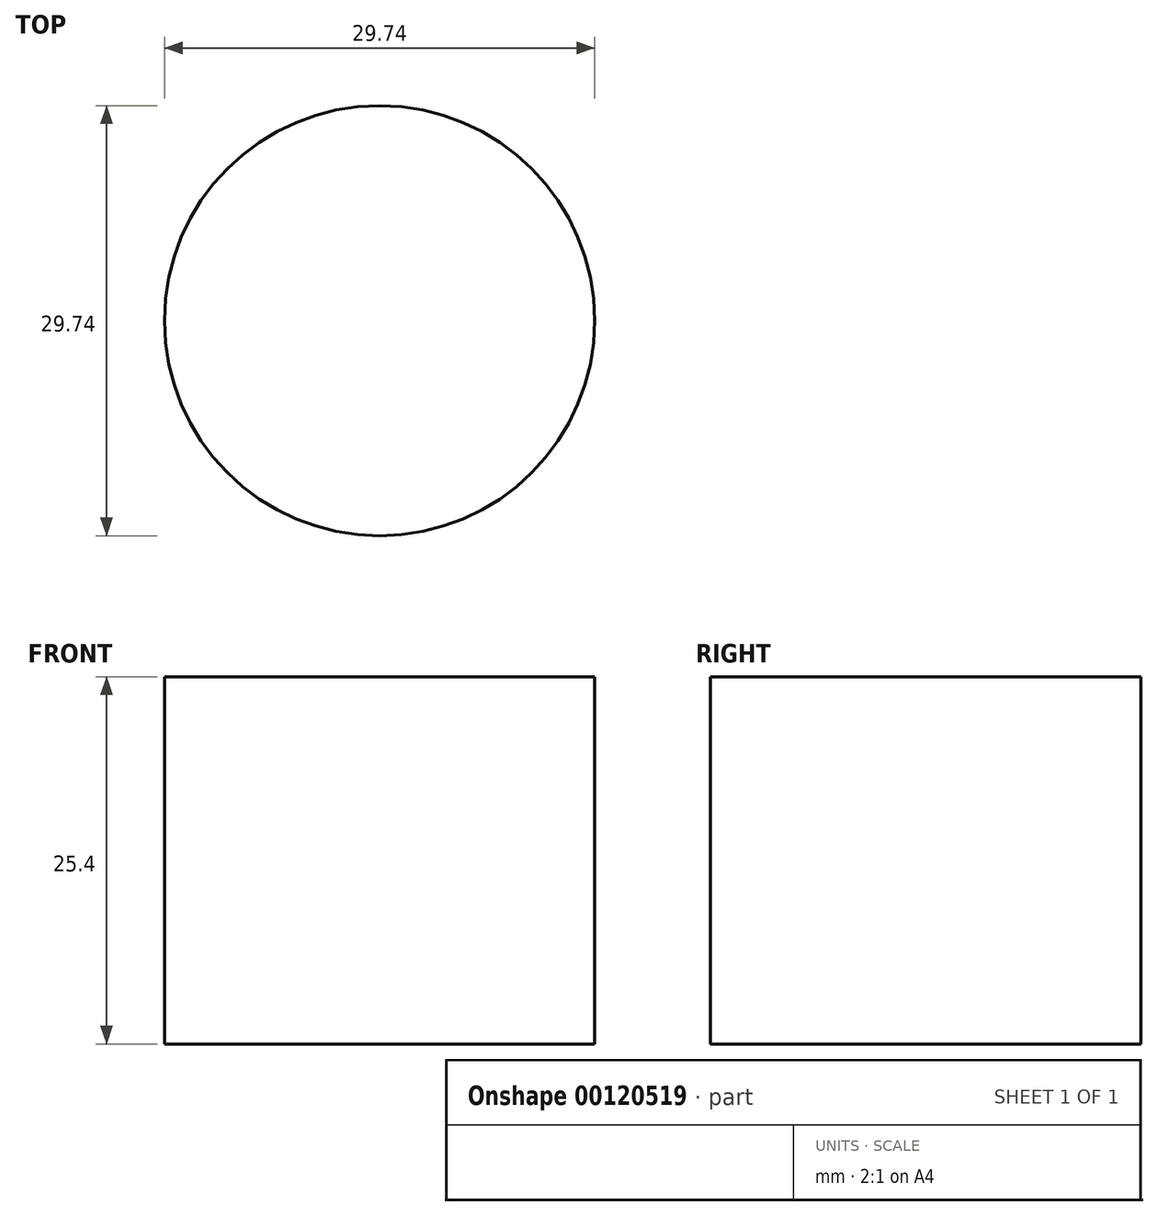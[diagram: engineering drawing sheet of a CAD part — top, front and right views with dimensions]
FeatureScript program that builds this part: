
annotation { "Feature Type Name" : "Feature", "Feature Type Description" : "" }
export const myFeature = defineFeature(function(context is Context, id is Id, definition is map)
    precondition{}
    {
        {
            var Q0;
            Q0=qCreatedBy(makeId("Top.planeOp"),FACE);
            var sketch = newSketch(context, id + "F0", { "sketchPlane" : qUnion([Q0])});
            skCircle(sketch, "E0", {"center": v(0, 0) * mm, "radius": 25.58 * mm});
            skSolve(sketch);
        }
        {
            var Q0;
            Q0 = qSketchRegion(id + "F0", true);
            var Q1;
            Q1=sQuery(id+"F0.wireOp",EDGE,"E0");
            extrude(context, id + "F1", {"entities" : qUnion([Q0]), "bodyType" : ToolBodyType.SURFACE, "surfaceEntities" : qUnion([Q1]), "depth" : 25.4 * mm});
        }
        {
            var Q0;
            Q0=qCreatedBy(makeId("Top.planeOp"),FACE);
            var sketch = newSketch(context, id + "F2", { "sketchPlane" : qUnion([Q0])});
            skCircle(sketch, "E1", {"center": v(0, 0) * mm, "radius": 14.87 * mm});
            skLineSegment(sketch, "E2", {"start": v(-11.52, -9.4) * mm, "end": v(-18.3, -18.15) * mm});
            skLineSegment(sketch, "E3", {"start": v(0, -14.87) * mm, "end": v(0, -25.41) * mm});
            skLineSegment(sketch, "E4", {"start": v(13.07, -9.44) * mm, "end": v(20.04, -14.67) * mm});
            skLineSegment(sketch, "E5", {"start": v(14.87, 0) * mm, "end": v(25.56, 0) * mm});
            skLineSegment(sketch, "E6", {"start": v(11.54, 9.38) * mm, "end": v(18.3, 17.57) * mm});
            skLineSegment(sketch, "E7", {"start": v(0, 14.87) * mm, "end": v(0, 24.83) * mm});
            skLineSegment(sketch, "E8", {"start": v(-11.36, 9.6) * mm, "end": v(-18.88, 17.57) * mm});
            skLineSegment(sketch, "E9", {"start": v(-14.87, 0.18) * mm, "end": v(-25.85, 0) * mm});
            skSolve(sketch);
        }
        {
            var Q0;
            Q0 = qSketchRegion(id + "F2", true);
            var Q1;
            Q1=sQuery(id+"F2.wireOp",EDGE,"E9");
            var Q2;
            Q2=sQuery(id+"F2.wireOp",EDGE,"E2");
            var Q3;
            Q3=sQuery(id+"F2.wireOp",EDGE,"E4");
            var Q4;
            Q4=sQuery(id+"F2.wireOp",EDGE,"E5");
            var Q5;
            Q5=sQuery(id+"F2.wireOp",EDGE,"E6");
            var Q6;
            Q6=sQuery(id+"F2.wireOp",EDGE,"E7");
            var Q7;
            Q7=sQuery(id+"F2.wireOp",EDGE,"E8");
            var Q8;
            Q8=sQuery(id+"F2.wireOp",EDGE,"E3");
            extrude(context, id + "F3", {"entities" : qUnion([Q0]), "bodyType" : ToolBodyType.SURFACE, "surfaceEntities" : qUnion([Q1, Q2, Q3, Q4, Q5, Q6, Q7, Q8]), "depth" : 25.4 * mm});
        }
        {
            var Q0;
            Q0 = qSketchRegion(id + "F2", true);
            extrude(context, id + "F4", {"entities" : qUnion([Q0]), "depth" : 25.4 * mm});
        }
    });
